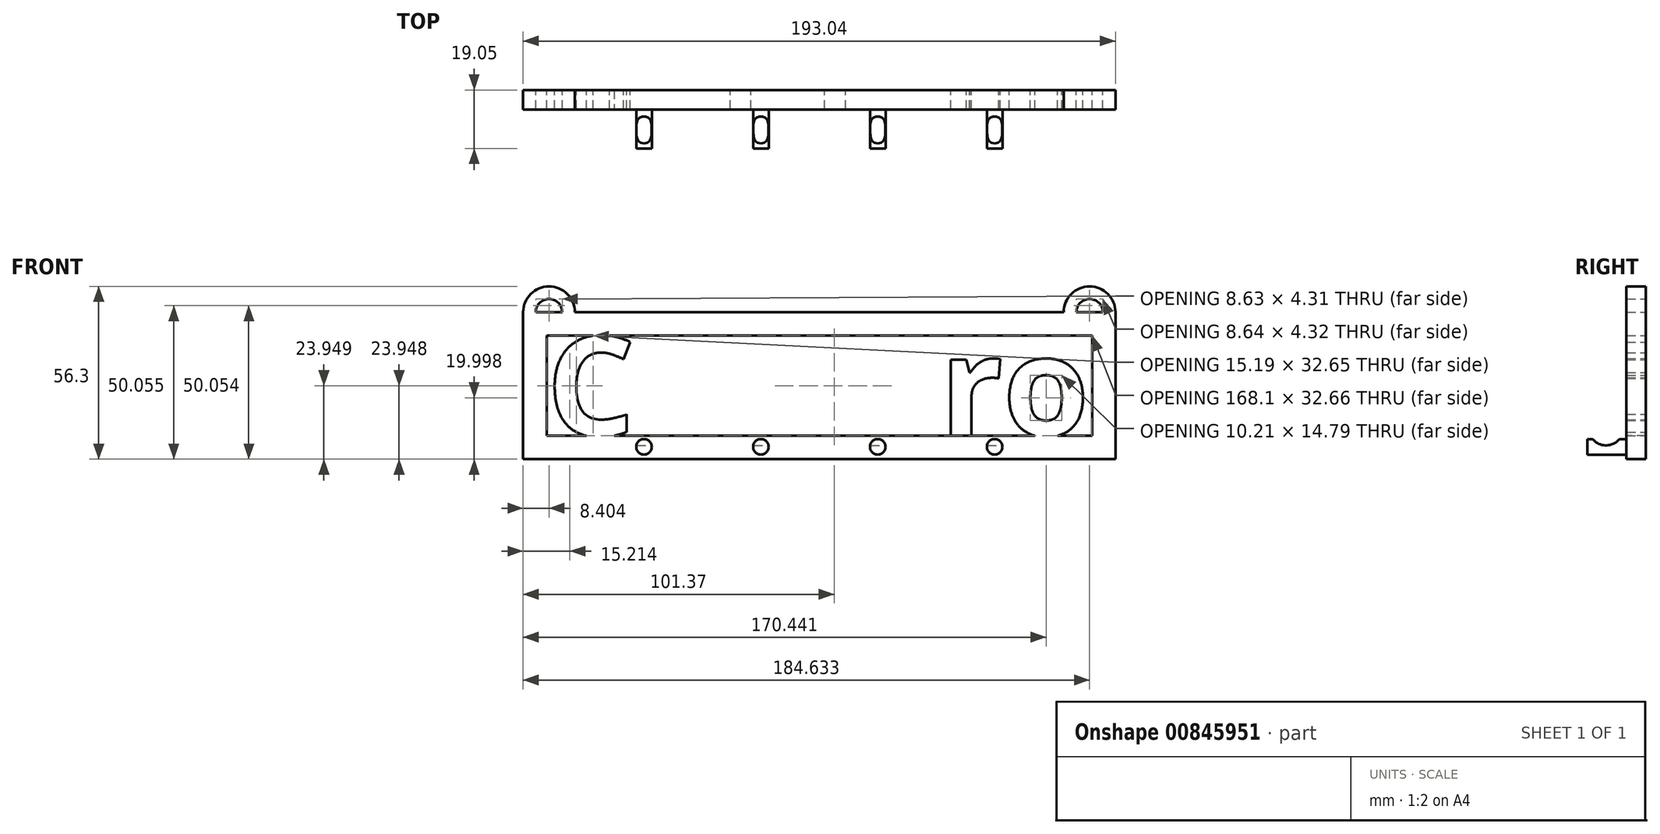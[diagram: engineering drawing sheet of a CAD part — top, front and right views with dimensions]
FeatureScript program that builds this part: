
annotation { "Feature Type Name" : "Feature", "Feature Type Description" : "" }
export const myFeature = defineFeature(function(context is Context, id is Id, definition is map)
    precondition{}
    {
        {
            var Q0;
            Q0=qCreatedBy(makeId("Front.planeOp"),FACE);
            var sketch = newSketch(context, id + "F0", { "sketchPlane" : qUnion([Q0])});
            skText(sketch, "E0", { "text": "Camaro", "fontName": "OpenSans-Bold.ttf"});
            skLineSegment(sketch, "E1", {"start": v(-88.9, 18.52) * mm, "end": v(88.9, 18.52) * mm});
            skLineSegment(sketch, "E2", {"start": v(88.9, -14.14) * mm, "end": v(88.9, 18.52) * mm});
            skLineSegment(sketch, "E3", {"start": v(88.9, -14.14) * mm, "end": v(-88.9, -14.14) * mm});
            skLineSegment(sketch, "E4", {"start": v(-88.9, 18.52) * mm, "end": v(-88.9, -14.14) * mm});
            skLineSegment(sketch, "E5", {"start": v(-96.52, 18.52) * mm, "end": v(-96.52, -21.76) * mm});
            skLineSegment(sketch, "E6", {"start": v(-96.52, -21.76) * mm, "end": v(96.52, -21.76) * mm});
            skLineSegment(sketch, "E7", {"start": v(96.52, -21.76) * mm, "end": v(96.52, 26.14) * mm});
            skLineSegment(sketch, "E8", {"start": v(96.52, 26.14) * mm, "end": v(-96.52, 26.14) * mm});
            skLineSegment(sketch, "E9", {"start": v(-96.52, 26.14) * mm, "end": v(-96.52, 18.52) * mm});
            skArc(sketch, "E10", {"start": v(-79.71, 26.14) * mm, "mid": v(-88.12, 34.54) * mm, "end": v(-96.52, 26.14) * mm});
            skArc(sketch, "E11", {"start": v(-83.8, 26.14) * mm, "mid": v(-88.12, 30.45) * mm, "end": v(-92.43, 26.14) * mm});
            skArc(sketch, "E12", {"start": v(96.52, 26.14) * mm, "mid": v(88.11, 34.54) * mm, "end": v(79.7, 26.14) * mm});
            skArc(sketch, "E13", {"start": v(92.43, 26.14) * mm, "mid": v(88.11, 30.45) * mm, "end": v(83.8, 26.14) * mm});
            const initialGuessF0  = {"E0": [-0.0889, -0.01414, 1, 0, 0.03265]};
            skSetInitialGuess(sketch, initialGuessF0);
            skSolve(sketch);
        }
        {
            var Q0;
            Q0 = qSketchRegion(id + "F0", true);
            var Q1;
            {var subQ0=sQuery(id+"F0.wireOp",EDGE,"E0.sketch_text.stroke-6");var subQ1=sQuery(id+"F0.wireOp",EDGE,"E0.sketch_text.stroke-5");var subQ2=makeQuery(id+"F0.imprint","INTERSECT",VERTEX,{"derivedFrom":[subQ1,subQ0]});Q1=makeQuery(id+"F0.imprint","IMPRINT",FACE,{"disambiguationData":[TD([[makeQuery(id+"F0.imprint","IMPRINT",EDGE,{"disambiguationData":[TD([[subQ2,1.0]])],"derivedFrom":subQ1}),-1.0]])]});}
            var Q2;
            Q2=makeQuery(id+"F0.imprint","IMPRINT",FACE,{"disambiguationData":[TD([[makeQuery(id+"F0.imprint","IMPRINT",EDGE,{"derivedFrom":sQuery(id+"F0.wireOp",EDGE,"E0.sketch_text.stroke-0")}),-1.0]])]});
            var Q3;
            {var subQ5=sQuery(id+"F0.wireOp",EDGE,"E0.sketch_text.stroke-15");Q3=makeQuery(id+"F0.imprint","IMPRINT",FACE,{"disambiguationData":[TD([[makeQuery(id+"F0.imprint","IMPRINT",EDGE,{"derivedFrom":subQ5}),-1.0]])]});}
            var Q4;
            {var subQ0=sQuery(id+"F0.wireOp",EDGE,"E0.sketch_text.stroke-19");var subQ1=sQuery(id+"F0.wireOp",EDGE,"E0.sketch_text.stroke-18");var subQ2=makeQuery(id+"F0.imprint","INTERSECT",VERTEX,{"derivedFrom":[subQ1,subQ0]});Q4=makeQuery(id+"F0.imprint","IMPRINT",FACE,{"disambiguationData":[TD([[makeQuery(id+"F0.imprint","IMPRINT",EDGE,{"disambiguationData":[TD([[subQ2,1.0]])],"derivedFrom":subQ1}),-1.0]])]});}
            var Q5;
            {var subQ3=sQuery(id+"F0.wireOp",EDGE,"E0.sketch_text.stroke-41");Q5=makeQuery(id+"F0.imprint","IMPRINT",FACE,{"disambiguationData":[TD([[makeQuery(id+"F0.imprint","IMPRINT",EDGE,{"derivedFrom":subQ3}),-1.0]])]});}
            var Q6;
            {var subQ5=sQuery(id+"F0.wireOp",EDGE,"E0.sketch_text.stroke-68");Q6=makeQuery(id+"F0.imprint","IMPRINT",FACE,{"disambiguationData":[TD([[makeQuery(id+"F0.imprint","IMPRINT",EDGE,{"derivedFrom":subQ5}),-1.0]])]});}
            var Q7;
            {var subQ0=sQuery(id+"F0.wireOp",EDGE,"E0.sketch_text.stroke-72");var subQ1=sQuery(id+"F0.wireOp",EDGE,"E0.sketch_text.stroke-71");var subQ2=makeQuery(id+"F0.imprint","INTERSECT",VERTEX,{"derivedFrom":[subQ1,subQ0]});Q7=makeQuery(id+"F0.imprint","IMPRINT",FACE,{"disambiguationData":[TD([[makeQuery(id+"F0.imprint","IMPRINT",EDGE,{"disambiguationData":[TD([[subQ2,1.0]])],"derivedFrom":subQ1}),-1.0]])]});}
            var Q8;
            Q8=makeQuery(id+"F0.imprint","IMPRINT",FACE,{"disambiguationData":[TD([[makeQuery(id+"F0.imprint","IMPRINT",EDGE,{"derivedFrom":sQuery(id+"F0.wireOp",EDGE,"E0.sketch_text.stroke-93")}),-1.0]])]});
            var Q9;
            Q9=makeQuery(id+"F0.imprint","IMPRINT",FACE,{"disambiguationData":[TD([[makeQuery(id+"F0.imprint","IMPRINT",EDGE,{"derivedFrom":sQuery(id+"F0.wireOp",EDGE,"E0.sketch_text.stroke-106")}),-1.0]])]});
            var Q10;
            {var subQ0=sQuery(id+"F0.wireOp",EDGE,"E0.sketch_text.stroke-116");var subQ1=sQuery(id+"F0.wireOp",EDGE,"E0.sketch_text.stroke-115");var subQ2=makeQuery(id+"F0.imprint","INTERSECT",VERTEX,{"derivedFrom":[subQ1,subQ0]});Q10=makeQuery(id+"F0.imprint","IMPRINT",FACE,{"disambiguationData":[TD([[makeQuery(id+"F0.imprint","IMPRINT",EDGE,{"disambiguationData":[TD([[subQ2,1.0]])],"derivedFrom":subQ1}),-1.0]])]});}
            var Q11;
            {var subQ0=sQuery(id+"F0.wireOp",EDGE,"E0.sketch_text.stroke-11");var subQ1=sQuery(id+"F0.wireOp",EDGE,"E0.sketch_text.stroke-10");var subQ2=makeQuery(id+"F0.imprint","INTERSECT",VERTEX,{"derivedFrom":[subQ1,subQ0]});Q11=makeQuery(id+"F0.imprint","IMPRINT",FACE,{"disambiguationData":[TD([[makeQuery(id+"F0.imprint","IMPRINT",EDGE,{"disambiguationData":[TD([[subQ2,1.0]])],"derivedFrom":subQ1}),-1.0]])]});}
            extrude(context, id + "F1", {"entities" : qUnion([Q0, Q1, Q2, Q3, Q4, Q5, Q6, Q7, Q8, Q9, Q10, Q11]), "depth" : 6.35 * mm, "offsetDistance" : 25.4 * mm});
        }
        {
            var Q0;
            Q0=makeQuery(id+"F1.opExtrude","CAP_FACE",FACE,{"disambiguationData":[OSD([sQuery(id+"F0.wireOp",EDGE,"E0.sketch_text.stroke-0"),sQuery(id+"F0.wireOp",EDGE,"E0.sketch_text.stroke-1"),sQuery(id+"F0.wireOp",EDGE,"E0.sketch_text.stroke-2"),sQuery(id+"F0.wireOp",EDGE,"E0.sketch_text.stroke-3"),sQuery(id+"F0.wireOp",EDGE,"E0.sketch_text.stroke-4"),sQuery(id+"F0.wireOp",EDGE,"E0.sketch_text.stroke-5"),sQuery(id+"F0.wireOp",EDGE,"E0.sketch_text.stroke-6"),sQuery(id+"F0.wireOp",EDGE,"E0.sketch_text.stroke-7"),sQuery(id+"F0.wireOp",EDGE,"E0.sketch_text.stroke-8"),sQuery(id+"F0.wireOp",EDGE,"E0.sketch_text.stroke-9"),sQuery(id+"F0.wireOp",EDGE,"E0.sketch_text.stroke-10"),sQuery(id+"F0.wireOp",EDGE,"E0.sketch_text.stroke-11"),sQuery(id+"F0.wireOp",EDGE,"E0.sketch_text.stroke-12"),sQuery(id+"F0.wireOp",EDGE,"E0.sketch_text.stroke-13"),sQuery(id+"F0.wireOp",EDGE,"E0.sketch_text.stroke-14"),sQuery(id+"F0.wireOp",EDGE,"E0.sketch_text.stroke-15"),sQuery(id+"F0.wireOp",EDGE,"E0.sketch_text.stroke-16"),sQuery(id+"F0.wireOp",EDGE,"E0.sketch_text.stroke-17"),sQuery(id+"F0.wireOp",EDGE,"E0.sketch_text.stroke-18"),sQuery(id+"F0.wireOp",EDGE,"E0.sketch_text.stroke-19"),sQuery(id+"F0.wireOp",EDGE,"E0.sketch_text.stroke-20"),sQuery(id+"F0.wireOp",EDGE,"E0.sketch_text.stroke-21"),sQuery(id+"F0.wireOp",EDGE,"E0.sketch_text.stroke-22"),sQuery(id+"F0.wireOp",EDGE,"E0.sketch_text.stroke-23"),sQuery(id+"F0.wireOp",EDGE,"E0.sketch_text.stroke-24"),sQuery(id+"F0.wireOp",EDGE,"E0.sketch_text.stroke-25"),sQuery(id+"F0.wireOp",EDGE,"E0.sketch_text.stroke-26"),sQuery(id+"F0.wireOp",EDGE,"E0.sketch_text.stroke-27"),sQuery(id+"F0.wireOp",EDGE,"E0.sketch_text.stroke-28"),sQuery(id+"F0.wireOp",EDGE,"E0.sketch_text.stroke-29"),sQuery(id+"F0.wireOp",EDGE,"E0.sketch_text.stroke-30"),sQuery(id+"F0.wireOp",EDGE,"E0.sketch_text.stroke-31"),sQuery(id+"F0.wireOp",EDGE,"E0.sketch_text.stroke-33"),sQuery(id+"F0.wireOp",EDGE,"E0.sketch_text.stroke-34"),sQuery(id+"F0.wireOp",EDGE,"E0.sketch_text.stroke-35"),sQuery(id+"F0.wireOp",EDGE,"E0.sketch_text.stroke-36"),sQuery(id+"F0.wireOp",EDGE,"E0.sketch_text.stroke-37"),sQuery(id+"F0.wireOp",EDGE,"E0.sketch_text.stroke-38"),sQuery(id+"F0.wireOp",EDGE,"E0.sketch_text.stroke-39"),sQuery(id+"F0.wireOp",EDGE,"E0.sketch_text.stroke-41"),sQuery(id+"F0.wireOp",EDGE,"E0.sketch_text.stroke-42"),sQuery(id+"F0.wireOp",EDGE,"E0.sketch_text.stroke-43"),sQuery(id+"F0.wireOp",EDGE,"E0.sketch_text.stroke-44"),sQuery(id+"F0.wireOp",EDGE,"E0.sketch_text.stroke-45"),sQuery(id+"F0.wireOp",EDGE,"E0.sketch_text.stroke-46"),sQuery(id+"F0.wireOp",EDGE,"E0.sketch_text.stroke-48"),sQuery(id+"F0.wireOp",EDGE,"E0.sketch_text.stroke-49"),sQuery(id+"F0.wireOp",EDGE,"E0.sketch_text.stroke-50"),sQuery(id+"F0.wireOp",EDGE,"E0.sketch_text.stroke-51"),sQuery(id+"F0.wireOp",EDGE,"E0.sketch_text.stroke-52"),sQuery(id+"F0.wireOp",EDGE,"E0.sketch_text.stroke-53"),sQuery(id+"F0.wireOp",EDGE,"E0.sketch_text.stroke-54"),sQuery(id+"F0.wireOp",EDGE,"E0.sketch_text.stroke-55"),sQuery(id+"F0.wireOp",EDGE,"E0.sketch_text.stroke-56"),sQuery(id+"F0.wireOp",EDGE,"E0.sketch_text.stroke-57"),sQuery(id+"F0.wireOp",EDGE,"E0.sketch_text.stroke-58"),sQuery(id+"F0.wireOp",EDGE,"E0.sketch_text.stroke-59"),sQuery(id+"F0.wireOp",EDGE,"E0.sketch_text.stroke-60"),sQuery(id+"F0.wireOp",EDGE,"E0.sketch_text.stroke-62"),sQuery(id+"F0.wireOp",EDGE,"E0.sketch_text.stroke-63"),sQuery(id+"F0.wireOp",EDGE,"E0.sketch_text.stroke-64"),sQuery(id+"F0.wireOp",EDGE,"E0.sketch_text.stroke-65"),sQuery(id+"F0.wireOp",EDGE,"E0.sketch_text.stroke-66"),sQuery(id+"F0.wireOp",EDGE,"E0.sketch_text.stroke-67"),sQuery(id+"F0.wireOp",EDGE,"E0.sketch_text.stroke-68"),sQuery(id+"F0.wireOp",EDGE,"E0.sketch_text.stroke-69"),sQuery(id+"F0.wireOp",EDGE,"E0.sketch_text.stroke-70"),sQuery(id+"F0.wireOp",EDGE,"E0.sketch_text.stroke-71"),sQuery(id+"F0.wireOp",EDGE,"E0.sketch_text.stroke-72"),sQuery(id+"F0.wireOp",EDGE,"E0.sketch_text.stroke-73"),sQuery(id+"F0.wireOp",EDGE,"E0.sketch_text.stroke-74"),sQuery(id+"F0.wireOp",EDGE,"E0.sketch_text.stroke-75"),sQuery(id+"F0.wireOp",EDGE,"E0.sketch_text.stroke-76"),sQuery(id+"F0.wireOp",EDGE,"E0.sketch_text.stroke-77"),sQuery(id+"F0.wireOp",EDGE,"E0.sketch_text.stroke-78"),sQuery(id+"F0.wireOp",EDGE,"E0.sketch_text.stroke-79"),sQuery(id+"F0.wireOp",EDGE,"E0.sketch_text.stroke-80"),sQuery(id+"F0.wireOp",EDGE,"E0.sketch_text.stroke-81"),sQuery(id+"F0.wireOp",EDGE,"E0.sketch_text.stroke-82"),sQuery(id+"F0.wireOp",EDGE,"E0.sketch_text.stroke-83"),sQuery(id+"F0.wireOp",EDGE,"E0.sketch_text.stroke-84"),sQuery(id+"F0.wireOp",EDGE,"E0.sketch_text.stroke-86"),sQuery(id+"F0.wireOp",EDGE,"E0.sketch_text.stroke-87"),sQuery(id+"F0.wireOp",EDGE,"E0.sketch_text.stroke-88"),sQuery(id+"F0.wireOp",EDGE,"E0.sketch_text.stroke-89"),sQuery(id+"F0.wireOp",EDGE,"E0.sketch_text.stroke-90"),sQuery(id+"F0.wireOp",EDGE,"E0.sketch_text.stroke-91"),sQuery(id+"F0.wireOp",EDGE,"E0.sketch_text.stroke-92"),sQuery(id+"F0.wireOp",EDGE,"E0.sketch_text.stroke-93"),sQuery(id+"F0.wireOp",EDGE,"E0.sketch_text.stroke-94"),sQuery(id+"F0.wireOp",EDGE,"E0.sketch_text.stroke-95"),sQuery(id+"F0.wireOp",EDGE,"E0.sketch_text.stroke-96"),sQuery(id+"F0.wireOp",EDGE,"E0.sketch_text.stroke-97"),sQuery(id+"F0.wireOp",EDGE,"E0.sketch_text.stroke-98"),sQuery(id+"F0.wireOp",EDGE,"E0.sketch_text.stroke-100"),sQuery(id+"F0.wireOp",EDGE,"E0.sketch_text.stroke-101"),sQuery(id+"F0.wireOp",EDGE,"E0.sketch_text.stroke-102"),sQuery(id+"F0.wireOp",EDGE,"E0.sketch_text.stroke-103"),sQuery(id+"F0.wireOp",EDGE,"E0.sketch_text.stroke-104"),sQuery(id+"F0.wireOp",EDGE,"E0.sketch_text.stroke-105"),sQuery(id+"F0.wireOp",EDGE,"E0.sketch_text.stroke-106"),sQuery(id+"F0.wireOp",EDGE,"E0.sketch_text.stroke-107"),sQuery(id+"F0.wireOp",EDGE,"E0.sketch_text.stroke-108"),sQuery(id+"F0.wireOp",EDGE,"E0.sketch_text.stroke-109"),sQuery(id+"F0.wireOp",EDGE,"E0.sketch_text.stroke-110"),sQuery(id+"F0.wireOp",EDGE,"E0.sketch_text.stroke-111"),sQuery(id+"F0.wireOp",EDGE,"E0.sketch_text.stroke-112"),sQuery(id+"F0.wireOp",EDGE,"E0.sketch_text.stroke-113"),sQuery(id+"F0.wireOp",EDGE,"E0.sketch_text.stroke-114"),sQuery(id+"F0.wireOp",EDGE,"E0.sketch_text.stroke-115"),sQuery(id+"F0.wireOp",EDGE,"E0.sketch_text.stroke-116"),sQuery(id+"F0.wireOp",EDGE,"E0.sketch_text.stroke-117"),sQuery(id+"F0.wireOp",EDGE,"E0.sketch_text.stroke-118"),sQuery(id+"F0.wireOp",EDGE,"E0.sketch_text.stroke-119"),sQuery(id+"F0.wireOp",EDGE,"E0.sketch_text.stroke-120"),sQuery(id+"F0.wireOp",EDGE,"E0.sketch_text.stroke-121"),sQuery(id+"F0.wireOp",EDGE,"E0.sketch_text.stroke-122"),sQuery(id+"F0.wireOp",EDGE,"E0.sketch_text.stroke-123"),sQuery(id+"F0.wireOp",EDGE,"E1"),sQuery(id+"F0.wireOp",EDGE,"E2"),sQuery(id+"F0.wireOp",EDGE,"E3"),sQuery(id+"F0.wireOp",EDGE,"E4"),sQuery(id+"F0.wireOp",EDGE,"E5"),sQuery(id+"F0.wireOp",EDGE,"E6"),sQuery(id+"F0.wireOp",EDGE,"E7"),sQuery(id+"F0.wireOp",EDGE,"E8"),sQuery(id+"F0.wireOp",EDGE,"E9")])],"isStart":false});
            cPlane(context, id + "F2", {"entities" : qUnion([Q0]), "cplaneType" : CPlaneType.OFFSET, "offset" : 0 * mm, "width" : 152.4 * mm, "height" : 152.4 * mm});
        }
        {
            var Q0;
            Q0=qCreatedBy(id+"F2.planeOp",FACE);
            var sketch = newSketch(context, id + "F3", { "sketchPlane" : qUnion([Q0])});
            skCircle(sketch, "E14", {"center": v(-57.15, -17.73) * mm, "radius": 2.54 * mm});
            skCircle(sketch, "E15", {"center": v(-19.05, -17.73) * mm, "radius": 2.54 * mm});
            skCircle(sketch, "E16", {"center": v(19.05, -17.73) * mm, "radius": 2.54 * mm});
            skCircle(sketch, "E17", {"center": v(57.15, -17.73) * mm, "radius": 2.54 * mm});
            skSolve(sketch);
        }
        {
            var Q0;
            Q0 = qSketchRegion(id + "F3", true);
            extrude(context, id + "F4", {"entities" : qUnion([Q0]), "operationType" : NewBodyOperationType.ADD, "depth" : 12.7 * mm, "offsetDistance" : 25.4 * mm});
        }
        {
            var Q0;
            Q0=qCreatedBy(makeId("Right.planeOp"),FACE);
            var sketch = newSketch(context, id + "F5", { "sketchPlane" : qUnion([Q0])});
            skCircle(sketch, "E18", {"center": v(-13, -11.52) * mm, "radius": 5.73 * mm});
            skSolve(sketch);
        }
        {
            var Q0;
            Q0 = qSketchRegion(id + "F5", true);
            extrude(context, id + "F6", {"entities" : qUnion([Q0]), "operationType" : NewBodyOperationType.REMOVE, "endBound" : BoundingType.SYMMETRIC, "oppositeDirection" : true, "depth" : 123.44 * mm, "offsetDistance" : 25.4 * mm});
        }
    });
